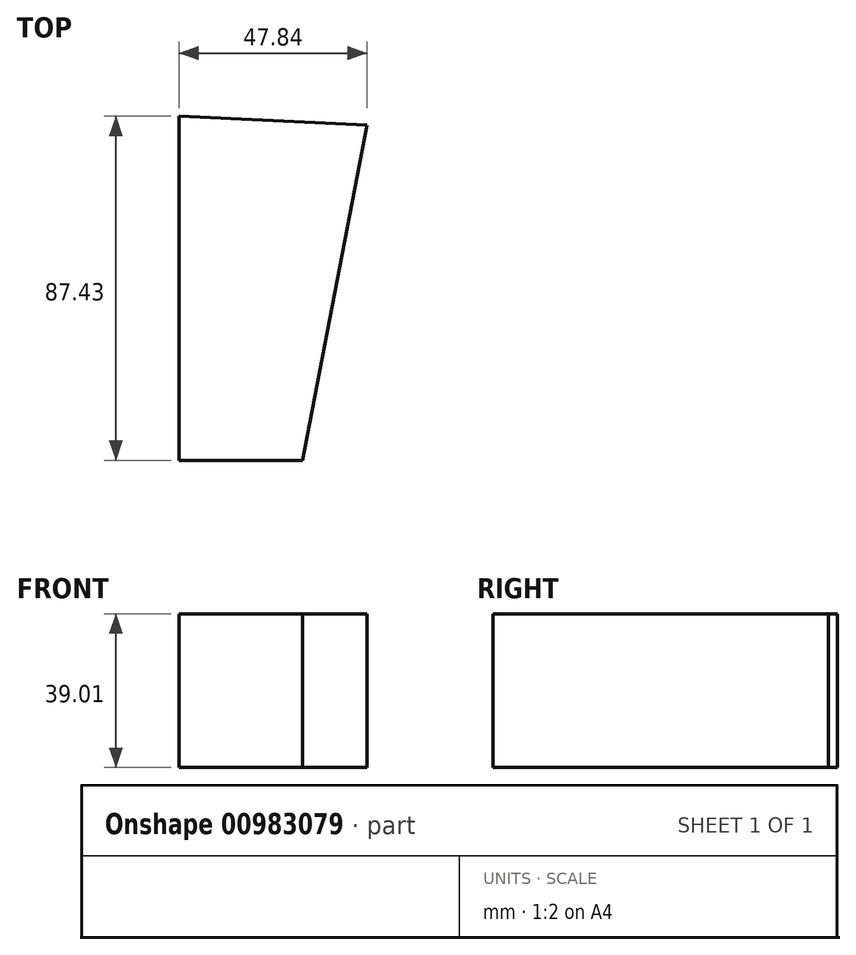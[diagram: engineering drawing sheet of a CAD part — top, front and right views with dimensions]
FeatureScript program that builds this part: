
annotation { "Feature Type Name" : "Feature", "Feature Type Description" : "" }
export const myFeature = defineFeature(function(context is Context, id is Id, definition is map)
    precondition{}
    {
        {
            var Q0;
            Q0=qCreatedBy(makeId("Top.planeOp"),FACE);
            var sketch = newSketch(context, id + "F0", { "sketchPlane" : qUnion([Q0])});
            skLineSegment(sketch, "E0", {"start": v(47.84, 45.14) * mm, "end": v(31.35, -40.04) * mm});
            skLineSegment(sketch, "E1", {"start": v(31.35, -40.04) * mm, "end": v(0, -40.04) * mm});
            skLineSegment(sketch, "E2", {"start": v(0, 47.4) * mm, "end": v(47.84, 45.14) * mm});
            skLineSegment(sketch, "E3", {"start": v(0, 47.4) * mm, "end": v(0, -40.04) * mm});
            skSolve(sketch);
        }
        {
            var Q0;
            Q0=qSketchRegion(id+"F0",true);
            extrude(context, id + "F1", {"entities" : qUnion([Q0]), "depth" : 39 * mm, "offsetDistance" : 25.4 * mm});
        }
    });
